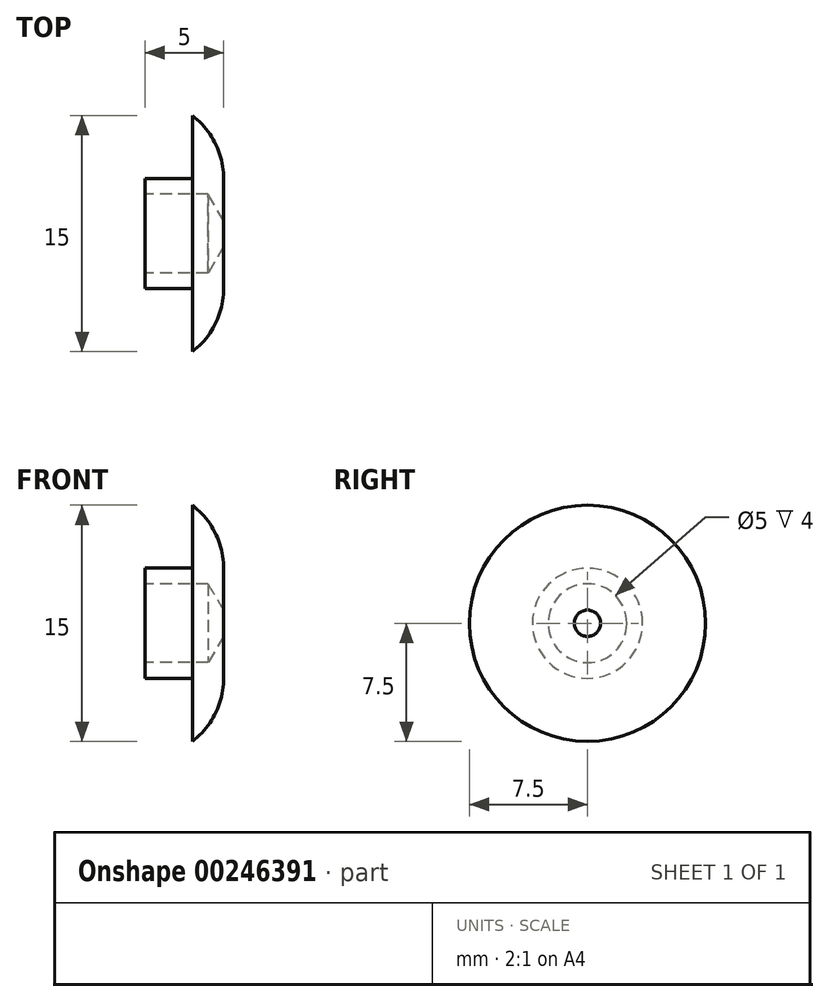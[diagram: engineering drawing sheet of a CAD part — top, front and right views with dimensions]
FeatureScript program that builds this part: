
annotation { "Feature Type Name" : "Feature", "Feature Type Description" : "" }
export const myFeature = defineFeature(function(context is Context, id is Id, definition is map)
    precondition{}
    {
        {
            var Q0;
            Q0=qCreatedBy(makeId("Front.planeOp"),FACE);
            var sketch = newSketch(context, id + "F0", { "sketchPlane" : qUnion([Q0])});
            skLineSegment(sketch, "E0", {"start": v(0, 3.5) * mm, "end": v(3, 3.5) * mm});
            skLineSegment(sketch, "E1", {"start": v(3, 3.5) * mm, "end": v(3, 7.5) * mm});
            skLineSegment(sketch, "E2", {"start": v(3, 7.5) * mm, "end": v(5, 7.5) * mm});
            skLineSegment(sketch, "E3", {"start": v(5, 7.5) * mm, "end": v(5, 0) * mm});
            skLineSegment(sketch, "E4", {"start": v(5, 0) * mm, "end": v(0, 0) * mm});
            skLineSegment(sketch, "E5", {"start": v(0, 3.5) * mm, "end": v(0, 0) * mm});
            skSolve(sketch);
        }
        {
            var Q0;
            Q0=makeQuery(id+"F0.imprint","IMPRINT",FACE,{"disambiguationData":[TD([[makeQuery(id+"F0.imprint","IMPRINT",EDGE,{"derivedFrom":sQuery(id+"F0.wireOp",EDGE,"E0")}),-1.0]])]});
            var Q1;
            Q1=sQuery(id+"F0.wireOp",EDGE,"E4");
            revolve(context, id + "F3", {"entities" : qUnion([Q0]), "axis" : qUnion([Q1]), "revolveType" : RevolveType.FULL});
        }
        {
            var Q0;
            Q0=makeQuery(id+"F3.opRevolve","SWEPT_FACE",FACE,{"disambiguationData":[OSD([sQuery(id+"F0.wireOp",EDGE,"E5")])]});
            var sketch = newSketch(context, id + "F1", { "sketchPlane" : qUnion([Q0])});
            skPoint(sketch, "E6", {"position": v(0, 0) * mm});
            skSolve(sketch);
        }
        {
            var Q0;
            Q0=sQuery(id+"F1.wireOp",VERTEX,"E6");
            var Q1;
            Q1=makeQuery(id+"F3.opRevolve","SWEPT_BODY",BODY,{"disambiguationData":[OSD([sQuery(id+"F0.wireOp",EDGE,"E0"),sQuery(id+"F0.wireOp",EDGE,"E1"),sQuery(id+"F0.wireOp",EDGE,"E2"),sQuery(id+"F0.wireOp",EDGE,"E3"),sQuery(id+"F0.wireOp",EDGE,"E4"),sQuery(id+"F0.wireOp",EDGE,"E5")])]});
            hole(context, id + "F4", {"style" : HoleStyle.SIMPLE, "endStyle" : HoleEndStyle.BLIND, "holeDiameter" : 5 * mm, "holeDepth" : 4 * mm, "tappedDepth" : 12.7 * mm, "tapClearance" : 3, "locations" : qUnion([Q0]), "scope" : qUnion([Q1])});
        }
        {
            var Q0;
            Q0=makeQuery(id+"F3.opRevolve","SWEPT_EDGE",EDGE,{"disambiguationData":[OSD([sQuery(id+"F0.wireOp",EDGE,"E2"),sQuery(id+"F0.wireOp",EDGE,"E3")])]});
            fillet(context, id + "F2", {"entities" : qUnion([Q0]), "radius" : 5.08 * mm, "tangentPropagation" : true, "allowEdgeOverflow" : false});
        }
    });
